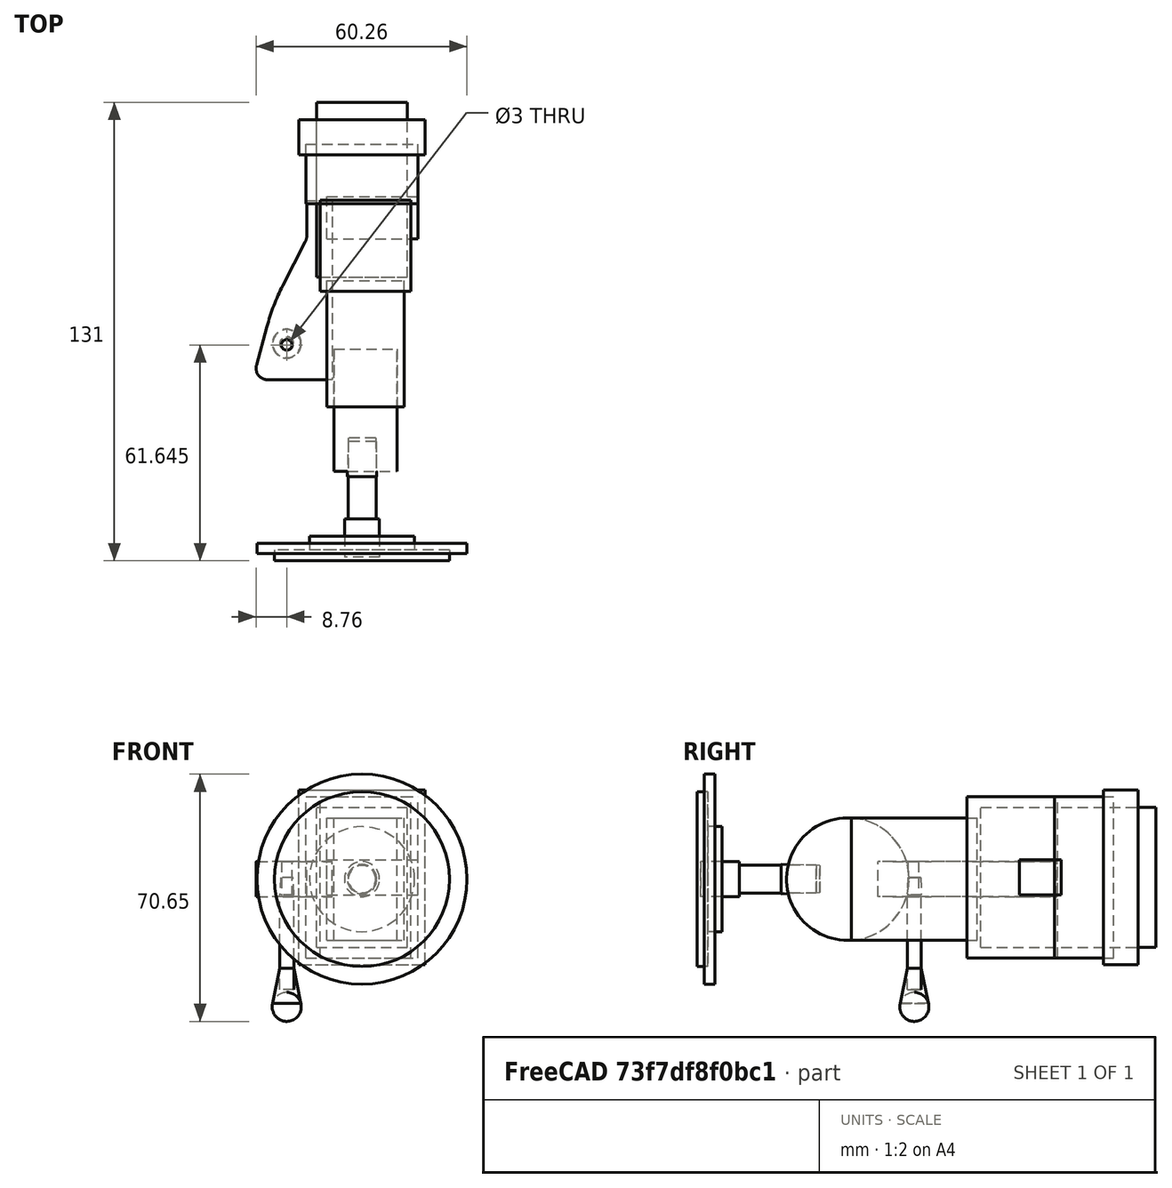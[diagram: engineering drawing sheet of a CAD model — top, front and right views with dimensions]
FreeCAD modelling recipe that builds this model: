
FCSTD DOCUMENT  (FreeCAD 0.16R6662 (Git))
Label: qtippholder-jw-rohbau
License: All rights reserved
LicenseURL: http://en.wikipedia.org/wiki/All_rights_reserved
objects: Part::Cylinder×7, Part::Box×6, Part::Cone×3, Mesh::Feature×1, Sketcher::SketchObject×1, PartDesign::Pad×1, Part::Sphere×1
note: 20 computed .brp shape members not serialized (recipe doc carries the construction recipe); baked Part::Feature solids carry a one-line shape summary decoded from their .brp

FEATURE [Mesh::Feature] EarClnrHldr
  Placement = pos=(1.7939,1.69608,-3.31283) rot=(0,0,1;0rad)
FEATURE [Part::Box] Box  label="hut"
  Height = 50
  Length = 36
  Placement = pos=(14,116,11) rot=(0,0,1;0rad)
  Width = 10
FEATURE [Part::Box] Box001  label="stirn"
  Height = 46
  Length = 32
  Placement = pos=(16,102,13) rot=(0,0,1;0rad)
  Width = 17
FEATURE [Part::Box] Box002  label="gnack"
  Height = 10
  Length = 26
  Placement = pos=(22,92,31) rot=(0,0,1;0rad)
  Width = 12
FEATURE [Part::Box] Box003  label="augen"
  Height = 46
  Length = 26
  Placement = pos=(20,77,13) rot=(0,0,1;0rad)
  Width = 26
FEATURE [Part::Box] Box004  label="wangen"
  Height = 35
  Length = 22
  Placement = pos=(22,44,18) rot=(0,0,1;0rad)
  Width = 36
FEATURE [Part::Cylinder] Cylinder  label="kinn"
  Angle = 360
  Height = 18
  Placement = pos=(24,43,35.5) rot=(0,1,0;1.5708rad)
  Radius = 17.5
FEATURE [Sketcher::SketchObject] Sketch001
  Placement = pos=(22,44,36) rot=(0,0,1;0rad)
  sketch-geometry (10):
    g0: LineSegment StartX=1.5 StartY=7.67084 StartZ=0 EndX=-16.9205 EndY=7.67084 EndZ=0
    g1: LineSegment StartX=-20.1462 StartY=11.8885 StartZ=0 EndX=-17.1712 EndY=22.8519 EndZ=0
    g2: LineSegment StartX=-12.6256 StartY=34.6 StartZ=0 EndX=-6.24014 EndY=47.0658 EndZ=0
    g3: LineSegment StartX=-5.70418 StartY=49.2877 StartZ=0 EndX=-5.70418 EndY=58.874 EndZ=0
    g4: LineSegment StartX=-5.70418 StartY=58.874 StartZ=0 EndX=1.5 EndY=58.874 EndZ=0
    g5: LineSegment StartX=1.5 StartY=58.874 StartZ=0 EndX=1.5 EndY=7.67084 EndZ=0
    g6: ArcOfCircle CenterX=-16.9205 CenterY=11.0132 CenterZ=0 NormalX=0 NormalY=0 NormalZ=1 Radius=3.34236 StartAngle=2.87662 EndAngle=4.71239
    g7: ArcOfCircle CenterX=41.2664 CenterY=6.99453 CenterZ=0 NormalX=0 NormalY=0 NormalZ=1 Radius=60.5508 StartAngle=2.6682 EndAngle=2.87662
    g8: ArcOfCircle CenterX=-10.5778 CenterY=49.2877 CenterZ=0 NormalX=0 NormalY=0 NormalZ=1 Radius=4.87365 StartAngle=5.8098 EndAngle=6.28319
    g9: Circle CenterX=-11.5 CenterY=17.6445 CenterZ=0 NormalX=0 NormalY=0 NormalZ=1 Radius=1.5
  constraints (14):
    c: Horizontal(g0)
    c: Vertical(g3)
    c: Coincident(g3,g4)
    c: Horizontal(g4)
    c: Coincident(g4,g5)
    c: Coincident(g5,g0)
    c: Vertical(g5)
    c: Tangent(g0,g6) = 1.5708
    c: Tangent(g1,g6) = 1.5708
    c: Tangent(g1,g7) = 1.5708
    c: Tangent(g2,g7) = 1.5708
    c: Tangent(g2,g8) = -1.5708
    c: Tangent(g3,g8) = -1.5708
    c: Radius(g9) = 1.5
FEATURE [PartDesign::Pad] Pad  label="nase"
  Length = 4.5
  Length2 = 5.5
  Placement = pos=(22,44,36) rot=(0,0,1;0rad)
  Sketch = -> Sketch001
  Type = 4
FEATURE [Part::Cylinder] Cylinder002  label="bein"
  Angle = 360
  Height = 32
  Placement = pos=(32,34,35.5) rot=(1,0,0;1.5708rad)
  Radius = 4
FEATURE [Part::Cylinder] Cylinder003  label="bein001"
  Angle = 360
  Height = 11
  Placement = pos=(32,12,35.5) rot=(1,0,0;1.5708rad)
  Radius = 5
FEATURE [Part::Cylinder] Cylinder004  label="bein002"
  Angle = 360
  Height = 4
  Placement = pos=(32,7,35.5) rot=(1,0,0;1.5708rad)
  Radius = 15
FEATURE [Part::Cylinder] Cylinder005  label="bein003"
  Angle = 360
  Height = 3
  Placement = pos=(32,5,35.5) rot=(1,0,0;1.5708rad)
  Radius = 30
FEATURE [Part::Cylinder] Cylinder006  label="bein004"
  Angle = 360
  Height = 3
  Placement = pos=(32,3,35.5) rot=(1,0,0;1.5708rad)
  Radius = 25
FEATURE [Part::Box] Box005  label="kopfloch"
  Height = 40
  Length = 26
  Placement = pos=(19,81,16) rot=(0,0,1;0rad)
  Width = 50
FEATURE [Part::Cylinder] Cylinder007  label="staebchen"
  Angle = 360
  Height = 27
  Placement = pos=(10.5,62,4) rot=(0,0,1;0rad)
  Radius = 2
FEATURE [Part::Sphere] Sphere  label="Kugel"
  Angle1 = -90
  Angle2 = 90
  Angle3 = 360
  Placement = pos=(10.5,62,-1) rot=(0,0,1;0rad)
  Radius = 4.15
FEATURE [Part::Cone] Cone  label="Kegel"
  Angle = 360
  Height = 10
  Placement = pos=(10.5,62,0) rot=(0,0,1;0rad)
  Radius1 = 4
  Radius2 = 2
FEATURE [Part::Cone] Cone001  label="Kegel001"
  Angle = 360
  Height = 5
  Placement = pos=(10.5,62,31) rot=(0,0,1;0rad)
  Radius1 = 2
  Radius2 = 1.8
FEATURE [Part::Cone] Cone002  label="beinloch001"
  Angle = 360
  Height = 11
  Placement = pos=(32,35,35.5) rot=(1,0,0;1.5708rad)
  Radius1 = 3.9
  Radius2 = 4.2
